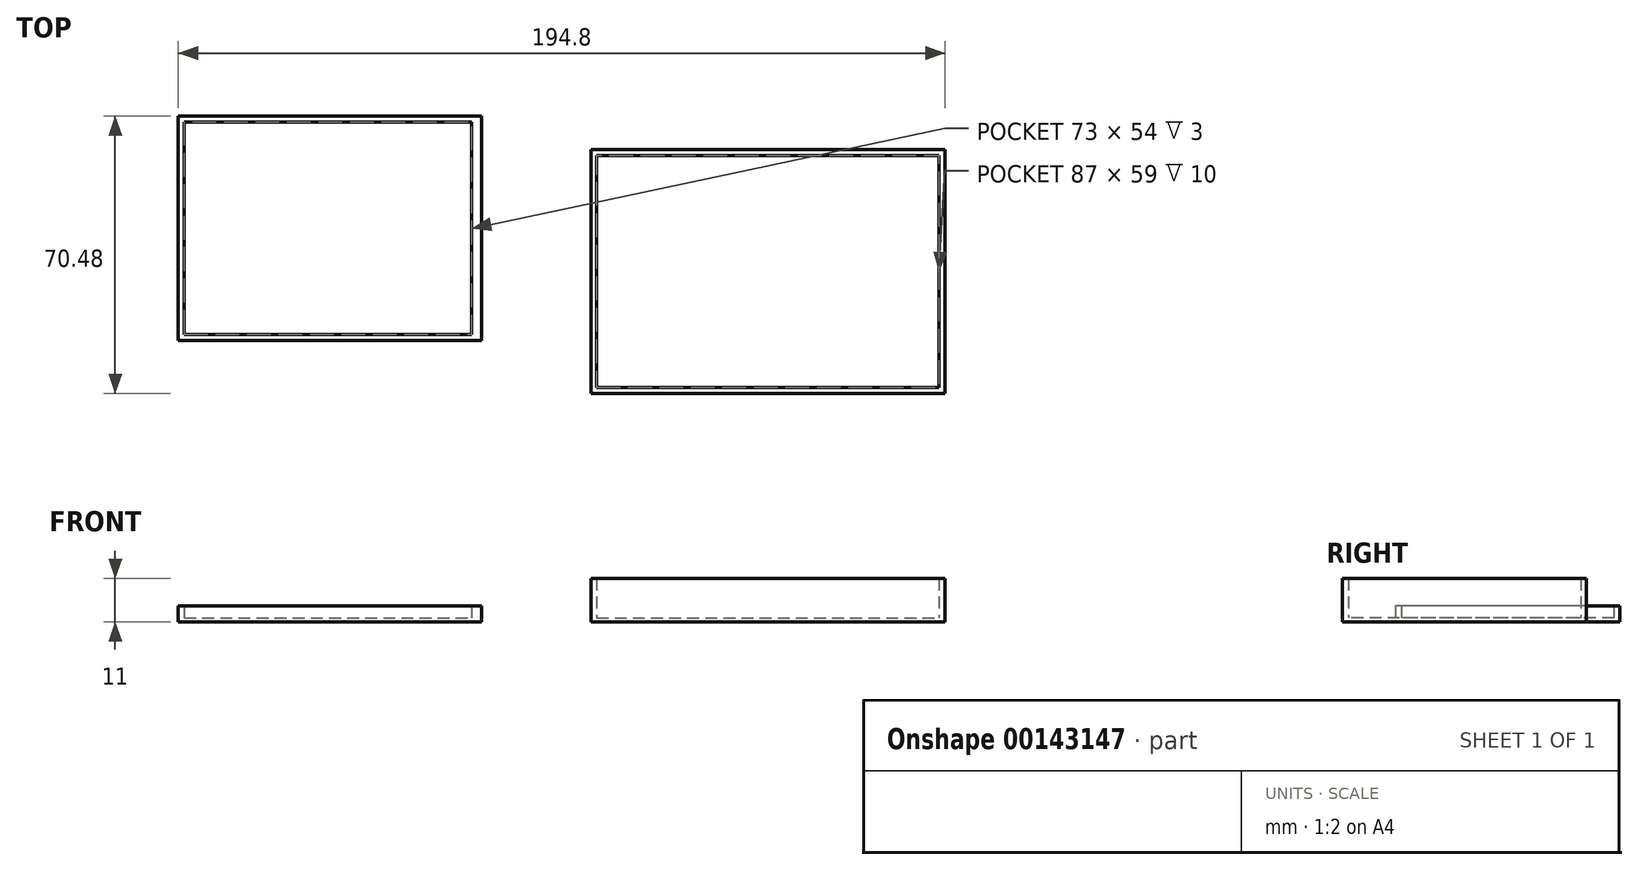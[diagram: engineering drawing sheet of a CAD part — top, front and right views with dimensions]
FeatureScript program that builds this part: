
annotation { "Feature Type Name" : "Feature", "Feature Type Description" : "" }
export const myFeature = defineFeature(function(context is Context, id is Id, definition is map)
    precondition{}
    {
        {
            var Q0;
            Q0=qCreatedBy(makeId("Top.planeOp"),FACE);
            var sketch = newSketch(context, id + "F0", { "sketchPlane" : qUnion([Q0])});
            skLineSegment(sketch, "E0.bottom", {"start": v(-33.46, 33.44) * mm, "end": v(56.54, 33.44) * mm});
            skLineSegment(sketch, "E0.top", {"start": v(-33.46, -28.56) * mm, "end": v(56.54, -28.56) * mm});
            skLineSegment(sketch, "E0.left", {"start": v(-33.46, 33.44) * mm, "end": v(-33.46, -28.56) * mm});
            skLineSegment(sketch, "E0.right", {"start": v(56.54, 33.44) * mm, "end": v(56.54, -28.56) * mm});
            skLineSegment(sketch, "E1.bottom", {"start": v(-31.96, 31.94) * mm, "end": v(55.04, 31.94) * mm});
            skLineSegment(sketch, "E1.top", {"start": v(-31.96, -27.06) * mm, "end": v(55.04, -27.06) * mm});
            skLineSegment(sketch, "E1.left", {"start": v(-31.96, 31.94) * mm, "end": v(-31.96, -27.06) * mm});
            skLineSegment(sketch, "E1.right", {"start": v(55.04, 31.94) * mm, "end": v(55.04, -27.06) * mm});
            skSolve(sketch);
        }
        {
            var Q0;
            Q0=makeQuery(id+"F0.imprint","IMPRINT",FACE,{"disambiguationData":[TD([[makeQuery(id+"F0.imprint","IMPRINT",EDGE,{"derivedFrom":sQuery(id+"F0.wireOp",EDGE,"E1.bottom")}),-1.0]])]});
            var Q1;
            Q1=makeQuery(id+"F0.imprint","IMPRINT",FACE,{"disambiguationData":[TD([[makeQuery(id+"F0.imprint","IMPRINT",EDGE,{"derivedFrom":sQuery(id+"F0.wireOp",EDGE,"E0.bottom")}),-1.0]])]});
            extrude(context, id + "F1", {"entities" : qUnion([Q0, Q1]), "depth" : 1 * mm});
        }
        {
            var Q0;
            Q0=makeQuery(id+"F1.opExtrude","CAP_FACE",FACE,{"disambiguationData":[OSD([sQuery(id+"F0.wireOp",EDGE,"E0.bottom"),sQuery(id+"F0.wireOp",EDGE,"E0.top"),sQuery(id+"F0.wireOp",EDGE,"E0.left"),sQuery(id+"F0.wireOp",EDGE,"E0.right")])],"isStart":false});
            var sketch = newSketch(context, id + "F2", { "sketchPlane" : qUnion([Q0])});
            skLineSegment(sketch, "E2.bottom", {"start": v(-31.96, 31.94) * mm, "end": v(55.04, 31.94) * mm});
            skLineSegment(sketch, "E2.top", {"start": v(-31.96, -27.06) * mm, "end": v(55.04, -27.06) * mm});
            skLineSegment(sketch, "E2.left", {"start": v(-31.96, 31.94) * mm, "end": v(-31.96, -27.06) * mm});
            skLineSegment(sketch, "E2.right", {"start": v(55.04, 31.94) * mm, "end": v(55.04, -27.06) * mm});
            skSolve(sketch);
        }
        {
            var Q0;
            Q0=makeQuery(id+"F2.imprint","IMPRINT",FACE,{"disambiguationData":[TD([[makeQuery(id+"F2.imprint","IMPRINT",EDGE,{"derivedFrom":sQuery(id+"F2.wireOp",EDGE,"E2.bottom")}),1.0]])]});
            extrude(context, id + "F3", {"entities" : qUnion([Q0]), "operationType" : NewBodyOperationType.ADD, "depth" : 10 * mm});
        }
        {
            var Q0;
            Q0=qCreatedBy(makeId("Top.planeOp"),FACE);
            var sketch = newSketch(context, id + "F4", { "sketchPlane" : qUnion([Q0])});
            skLineSegment(sketch, "E3.bottom", {"start": v(-138.26, 41.92) * mm, "end": v(-61.26, 41.92) * mm});
            skLineSegment(sketch, "E3.top", {"start": v(-138.26, -15.08) * mm, "end": v(-61.26, -15.08) * mm});
            skLineSegment(sketch, "E3.left", {"start": v(-138.26, 41.92) * mm, "end": v(-138.26, -15.08) * mm});
            skLineSegment(sketch, "E3.right", {"start": v(-61.26, 41.92) * mm, "end": v(-61.26, -15.08) * mm});
            skSolve(sketch);
        }
        {
            var Q0;
            Q0 = qSketchRegion(id + "F4", true);
            extrude(context, id + "F5", {"entities" : qUnion([Q0]), "depth" : 1 * mm});
        }
        {
            var Q0;
            Q0=makeQuery(id+"F5.opExtrude","CAP_FACE",FACE,{"disambiguationData":[OSD([sQuery(id+"F4.wireOp",EDGE,"E3.bottom"),sQuery(id+"F4.wireOp",EDGE,"E3.top"),sQuery(id+"F4.wireOp",EDGE,"E3.left"),sQuery(id+"F4.wireOp",EDGE,"E3.right")])],"isStart":false});
            var sketch = newSketch(context, id + "F6", { "sketchPlane" : qUnion([Q0])});
            skLineSegment(sketch, "E4.bottom", {"start": v(-136.76, 40.42) * mm, "end": v(-63.76, 40.42) * mm});
            skLineSegment(sketch, "E4.top", {"start": v(-136.76, -13.58) * mm, "end": v(-63.76, -13.58) * mm});
            skLineSegment(sketch, "E4.left", {"start": v(-136.76, 40.42) * mm, "end": v(-136.76, -13.58) * mm});
            skLineSegment(sketch, "E4.right", {"start": v(-63.76, 40.42) * mm, "end": v(-63.76, -13.58) * mm});
            skSolve(sketch);
        }
        {
            var Q0;
            Q0=makeQuery(id+"F6.imprint","IMPRINT",FACE,{"disambiguationData":[TD([[makeQuery(id+"F6.imprint","IMPRINT",EDGE,{"derivedFrom":sQuery(id+"F6.wireOp",EDGE,"E4.bottom")}),1.0]])]});
            extrude(context, id + "F7", {"entities" : qUnion([Q0]), "operationType" : NewBodyOperationType.ADD, "depth" : 3 * mm});
        }
    });
